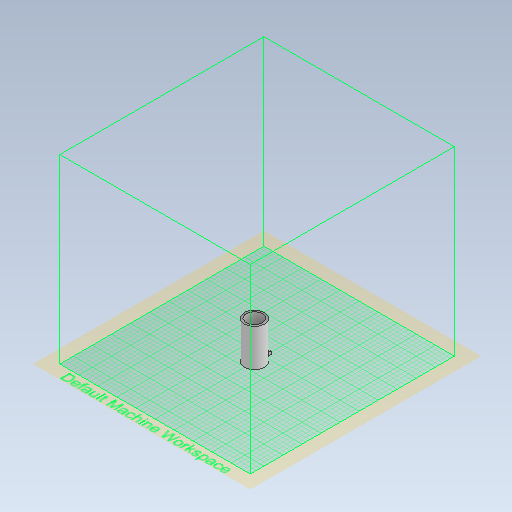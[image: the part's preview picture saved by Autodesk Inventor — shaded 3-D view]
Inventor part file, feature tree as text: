
AUTODESK INVENTOR PART (.ipt)
format: ipt  version: 2021 (Build 250183000, 183)  size: 417,280 bytes
history: native  units: in
note: dims shown in document units (in); Inventor stores cm internally (conversion verified against a paired STEP export)
features: extrude x3, sketch x3, fillet x1, chamfer x1, projected_geometry x1
ambient origin geometry x8: Origin, YZ Plane, XZ Plane, XY Plane, X Axis, Y Axis, Z Axis, Center Point
bodies: Solid1 (feature_tree)
feature tree (9):
  extrude  "Extrusion1"  Depth=3.2677in TaperAngle=0.0deg
  extrude  "Extrusion7"  Depth=3.2559in TaperAngle=0.0deg
  fillet  "Fillet12"  Radius=0.6693in
  extrude  "Extrusion15"  Depth=0.185in
  chamfer  "Chamfer9"  [1 undecoded]
  sketch  "Sketch2"  dims[d2=1.752in d3=3.2677in d4=0.0in]
  sketch  "Sketch9"  dims[d54=1.5945in d55=3.2559in d56=0.0in d117=0.6693in]
  projected_geometry  "Projected Loop7"
  sketch  "Sketch18"  dims[d122=0.122in d123=0.185in d124=0.0in d125=0.0in d130=0.1575in d131=0.0787in d132=45.0deg d19=0.0197in d20=0.0344in d21=0.0197in d22=0.0344in]
note: 1 required parameter value undecoded (feature->parameter linkage not recoverable at this tier; creation-order binding heuristic only, values carry confidence <= 0.55)
